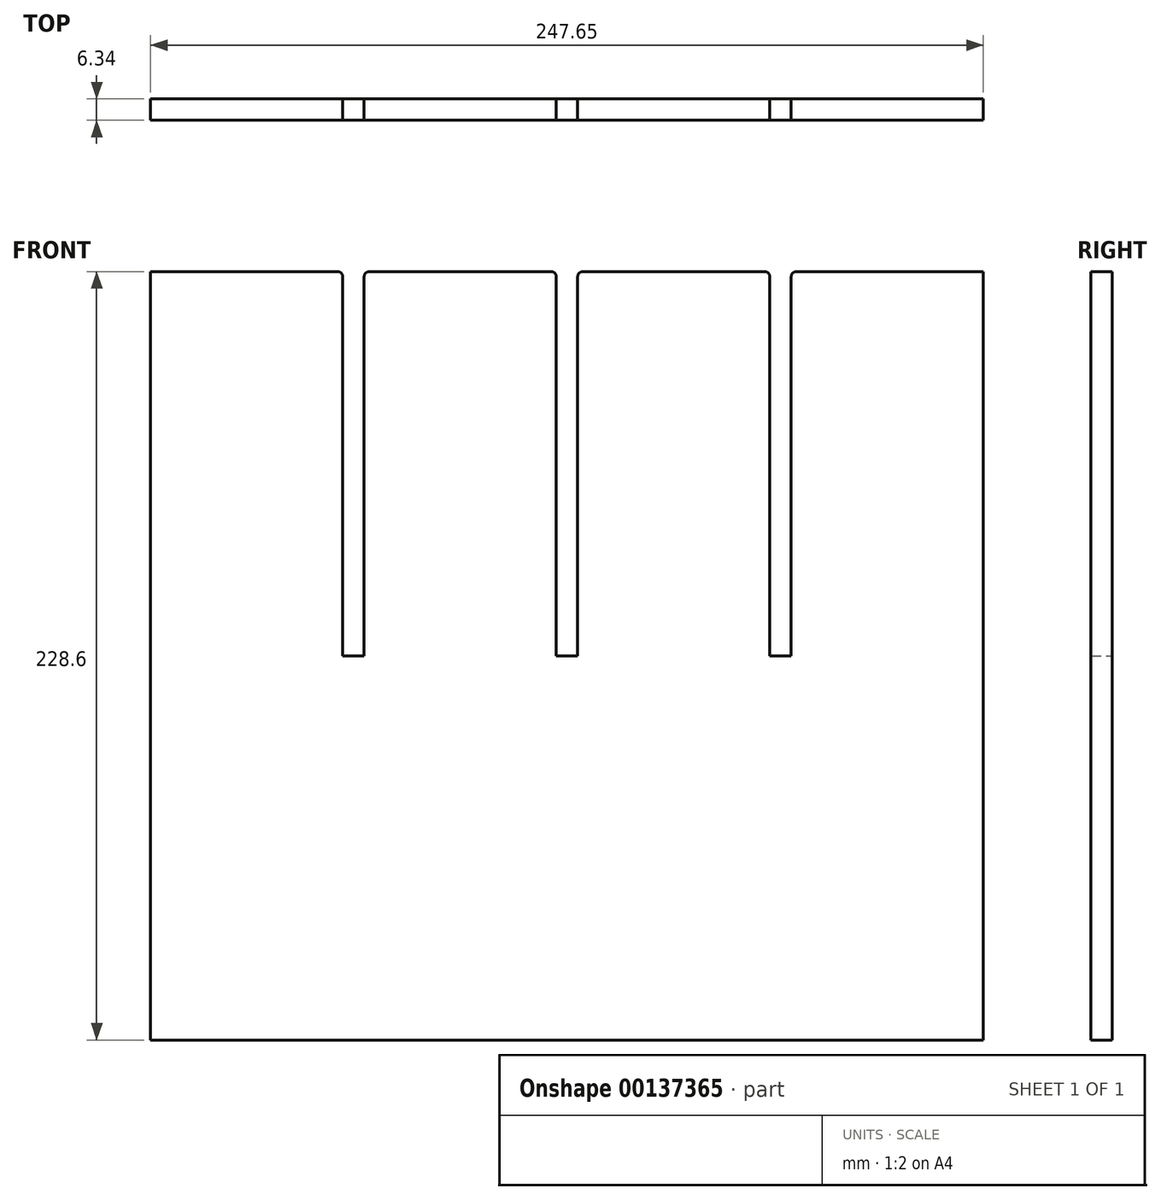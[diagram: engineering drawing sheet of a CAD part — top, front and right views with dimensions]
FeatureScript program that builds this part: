
annotation { "Feature Type Name" : "Feature", "Feature Type Description" : "" }
export const myFeature = defineFeature(function(context is Context, id is Id, definition is map)
    precondition{}
    {
        {
            var Q0;
            Q0=qCreatedBy(makeId("Front.planeOp"),FACE);
            var sketch = newSketch(context, id + "F0", { "sketchPlane" : qUnion([Q0])});
            skLineSegment(sketch, "E0.bottom", {"start": v(-128.59, 114.3) * mm, "end": v(-73.03, 114.3) * mm});
            skLineSegment(sketch, "E0.top", {"start": v(-128.59, -114.3) * mm, "end": v(119.06, -114.3) * mm});
            skLineSegment(sketch, "E0.left", {"start": v(-128.59, 114.3) * mm, "end": v(-128.59, -114.3) * mm});
            skLineSegment(sketch, "E1", {"start": v(119.06, 114.3) * mm, "end": v(119.06, -114.3) * mm});
            skLineSegment(sketch, "E2", {"start": v(-71.44, 112.71) * mm, "end": v(-71.44, 0) * mm});
            skLineSegment(sketch, "E3", {"start": v(-65.09, 0) * mm, "end": v(-65.09, 112.71) * mm});
            skLineSegment(sketch, "E4", {"start": v(-71.44, 0) * mm, "end": v(-65.09, 0) * mm});
            skLineSegment(sketch, "E5.trimOffspring", {"start": v(-63.5, 114.3) * mm, "end": v(-9.53, 114.3) * mm});
            skLineSegment(sketch, "E6.0.1.0", {"start": v(-1.59, 0) * mm, "end": v(-1.59, 112.71) * mm});
            skLineSegment(sketch, "E6.3.1.0", {"start": v(-7.94, 112.71) * mm, "end": v(-7.94, 0) * mm});
            skLineSegment(sketch, "E6.6.1.0", {"start": v(-7.94, 0) * mm, "end": v(-1.59, 0) * mm});
            skLineSegment(sketch, "E6.0.2.0", {"start": v(61.91, 0) * mm, "end": v(61.91, 112.71) * mm});
            skLineSegment(sketch, "E6.3.2.0", {"start": v(55.56, 112.71) * mm, "end": v(55.56, 0) * mm});
            skLineSegment(sketch, "E6.6.2.0", {"start": v(55.56, 0) * mm, "end": v(61.91, 0) * mm});
            skLineSegment(sketch, "E7.trimOffspring", {"start": v(0, 114.3) * mm, "end": v(53.97, 114.3) * mm});
            skLineSegment(sketch, "E8.trimOffspring", {"start": v(63.5, 114.3) * mm, "end": v(119.06, 114.3) * mm});
            skPoint(sketch, "E9.visualSharp", {"position": v(-71.44, 114.3) * mm});
            skArc(sketch, "E9.filletArc", {"start": v(-71.44, 112.71) * mm, "mid": v(-71.9, 113.84) * mm, "end": v(-73.03, 114.3) * mm});
            skPoint(sketch, "E10.visualSharp", {"position": v(-65.09, 114.3) * mm});
            skArc(sketch, "E10.filletArc", {"start": v(-63.5, 114.3) * mm, "mid": v(-64.62, 113.84) * mm, "end": v(-65.09, 112.71) * mm});
            skPoint(sketch, "E11.visualSharp", {"position": v(-7.94, 114.3) * mm});
            skArc(sketch, "E11.filletArc", {"start": v(-7.94, 112.71) * mm, "mid": v(-8.4, 113.84) * mm, "end": v(-9.53, 114.3) * mm});
            skPoint(sketch, "E12.visualSharp", {"position": v(-1.59, 114.3) * mm});
            skArc(sketch, "E12.filletArc", {"start": v(0, 114.3) * mm, "mid": v(-1.12, 113.84) * mm, "end": v(-1.59, 112.71) * mm});
            skPoint(sketch, "E13.visualSharp", {"position": v(55.56, 114.3) * mm});
            skArc(sketch, "E13.filletArc", {"start": v(55.56, 112.71) * mm, "mid": v(55.1, 113.84) * mm, "end": v(53.97, 114.3) * mm});
            skPoint(sketch, "E14.visualSharp", {"position": v(61.91, 114.3) * mm});
            skArc(sketch, "E14.filletArc", {"start": v(63.5, 114.3) * mm, "mid": v(62.38, 113.84) * mm, "end": v(61.91, 112.71) * mm});
            skSolve(sketch);
        }
        {
            var Q0;
            Q0 = qSketchRegion(id + "F0", true);
            extrude(context, id + "F1", {"entities" : qUnion([Q0]), "endBound" : BoundingType.SYMMETRIC, "depth" : 6.35 * mm});
        }
    });
